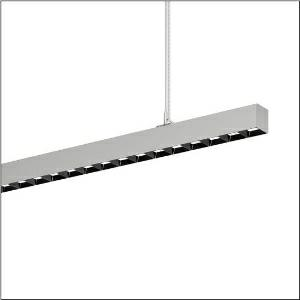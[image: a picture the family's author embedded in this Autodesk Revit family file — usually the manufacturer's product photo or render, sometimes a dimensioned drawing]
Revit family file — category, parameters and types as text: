
# Revit family: silica_r__21_51mx31tat7s_2b6e
name_source: partatom
category: Lighting Fixtures
units: mm (PartAtom-declared; Revit-internal decimal feet)

## family parameters
Cut with Voids When Loaded = No
Host = Face
Light Source = No
Part Type = Normal
Room Calculation Point = No
Round Connector Dimension = Use Diameter
Shared = No

## types (1)
- --- (1 x LED, 6220 lm, 53.5 W, 6500K)
    Apparent Load = 54 VA
    CIE Flux Codes = 85 99 100 60 100
    Color Rendering = 80
    Color Temperature = 6500K
    Default Elevation = 1800 mm
    Description = Silica® 21, office luminaire, primary light control with darklight reflector, of PMMA, black, CAT 2 (L<= 3000cd/m²), light emission: direct/indirect distribution, primary light characteristic: symmetric, installation type: suspended mounting, LED, rated luminous flux: 6.220lm, luminous efficacy: 111lm/W, light colour: 8tw, colour temperature: 2700..6500K, control gear: DALI DT8, with terminal, 3+2-pole, max. 2.5mm², mains connection: 220..240V, AC, 50/60Hz, rated input power: 56.2W, luminaire housing, of aluminium, metallic grey (RAL 9006), length: 1.204mm, width: 53mm, height: 53mm, protection rating (complete): IP20, insulation class (complete): insulation class I (protective earthing), certification: CE, permissible operating ambient temperature: 0..+35°C, standard: EN 50419, packaging unit: 1 piece
    Height = 53 mm
    Lamp = 1 x LED
    Lamp Light Flux = 6220 lm
    Lamp Power = 53.5 W
    Lamp count = 1
    Length = 1204 mm
    Luminous efficacy = 116 lm/W
    Manufacturer = Siteco
    ModVariant = No
    Model = 51MX31TAT7S
    Mounting Place = Ceiling
    Mounting Type = Pendant
    Number of Poles = 1
    OnlyDefault = Yes
    Power Factor = 1
    Product Name = Silica® 21
    Product group = office luminaire | ceiling pendant
    ProductGroupID = 904
    Protection Class = Protection class I
    Protection Degree = IP 20
    RLX_Detail_Level = 1
    RLX_Emergency_Light_Flux = 0 lm
    RLX_Emergency_Type = 0
    RLX_Emergency_Type_DB = No
    RlxData = <blob elided: 41197 chars, md5=f56f9c20>
    Socket = socket
    Standby Power = 0 W
    System Light Flux = 6220 lm
    System Power = 54 W
    Type Comments = individual setting
    Type Image = l_1335859.jpg
    URL = http://relux.com
    VarID = @adj_139872
    Voltage = 0 V
    Weight = 0.00 kg
    Width = 53 mm

## geometry (parser evidence)
native form markers: Blend x4, Sweep x13
no freeform markers — native parametric forms only
